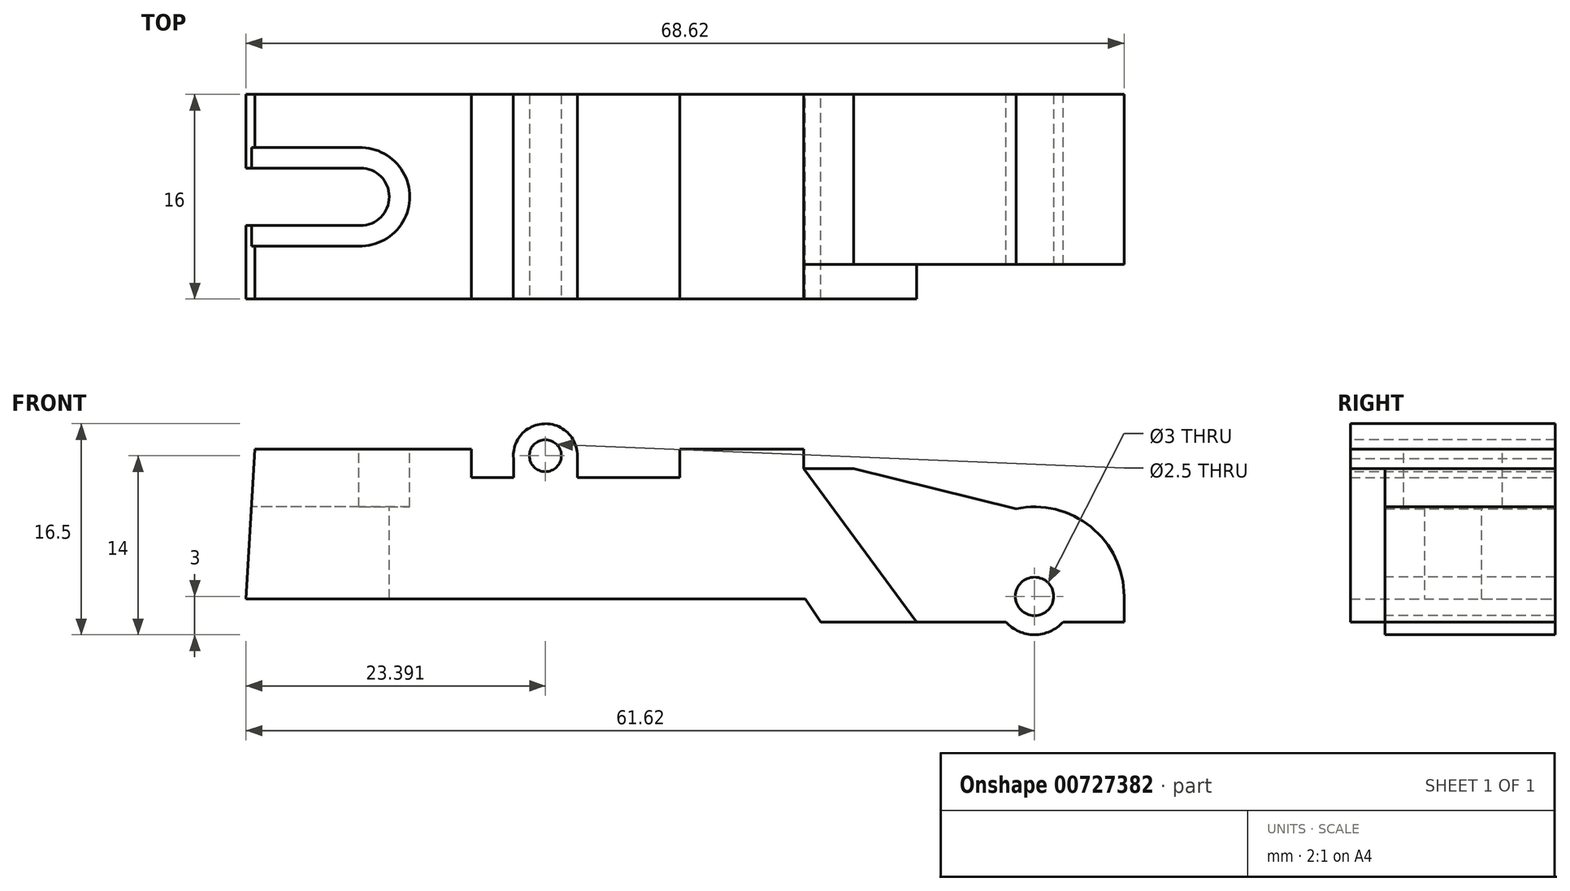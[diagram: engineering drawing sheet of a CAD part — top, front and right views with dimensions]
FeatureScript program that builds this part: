
annotation { "Feature Type Name" : "Feature", "Feature Type Description" : "" }
export const myFeature = defineFeature(function(context is Context, id is Id, definition is map)
    precondition{}
    {
        {
            var Q0;
            Q0=qCreatedBy(makeId("Front.planeOp"),FACE);
            var sketch = newSketch(context, id + "F0", { "sketchPlane" : qUnion([Q0])});
            skLineSegment(sketch, "E0", {"start": v(0, 0) * mm, "end": v(43.7, 0) * mm});
            skLineSegment(sketch, "E1", {"start": v(43.7, 0) * mm, "end": v(44.92, -1.8) * mm});
            skLineSegment(sketch, "E2", {"start": v(44.92, -1.8) * mm, "end": v(59.38, -1.8) * mm});
            skLineSegment(sketch, "E3", {"start": v(68.62, -1.8) * mm, "end": v(68.62, 0.65) * mm});
            skLineSegment(sketch, "E4", {"start": v(47.5, 10.2) * mm, "end": v(43.6, 10.2) * mm});
            skLineSegment(sketch, "E5", {"start": v(43.6, 10.2) * mm, "end": v(43.6, 11.7) * mm});
            skLineSegment(sketch, "E6", {"start": v(43.6, 11.7) * mm, "end": v(33.9, 11.7) * mm});
            skLineSegment(sketch, "E7", {"start": v(33.9, 11.7) * mm, "end": v(33.9, 9.5) * mm});
            skLineSegment(sketch, "E8", {"start": v(33.9, 9.5) * mm, "end": v(25.9, 9.5) * mm});
            skLineSegment(sketch, "E9", {"start": v(25.9, 9.5) * mm, "end": v(25.9, 11.2) * mm});
            skArc(sketch, "E10", {"start": v(25.9, 11.2) * mm, "mid": v(23.28, 13.7) * mm, "end": v(20.9, 10.99) * mm});
            skLineSegment(sketch, "E11", {"start": v(20.9, 10.99) * mm, "end": v(20.9, 9.5) * mm});
            skLineSegment(sketch, "E12", {"start": v(20.9, 9.5) * mm, "end": v(17.6, 9.5) * mm});
            skLineSegment(sketch, "E13", {"start": v(17.6, 9.5) * mm, "end": v(17.6, 11.7) * mm});
            skLineSegment(sketch, "E14", {"start": v(17.6, 11.7) * mm, "end": v(0.7, 11.7) * mm});
            skLineSegment(sketch, "E15", {"start": v(0.7, 11.7) * mm, "end": v(0, 0) * mm});
            skArc(sketch, "E16", {"start": v(68.62, 0.2) * mm, "mid": v(66.03, 5.64) * mm, "end": v(60.18, 7.05) * mm});
            skLineSegment(sketch, "E17", {"start": v(47.5, 10.2) * mm, "end": v(60.18, 7.05) * mm});
            skArc(sketch, "E18", {"start": v(59.38, -1.8) * mm, "mid": v(61.62, -2.8) * mm, "end": v(63.86, -1.8) * mm});
            skLineSegment(sketch, "E19.trimOffspring", {"start": v(63.86, -1.8) * mm, "end": v(68.62, -1.8) * mm});
            skSolve(sketch);
        }
        {
            var Q0;
            Q0=qSketchRegion(id+"F0",true);
            extrude(context, id + "F1", {"entities" : qUnion([Q0]), "depth" : 16 * mm, "offsetDistance" : 25 * mm});
        }
        {
            var Q0;
            Q0=makeQuery(id+"F1.opExtrude","CAP_FACE",FACE,{"disambiguationData":[OSD([sQuery(id+"F0.wireOp",EDGE,"E0"),sQuery(id+"F0.wireOp",EDGE,"E1"),sQuery(id+"F0.wireOp",EDGE,"E2"),sQuery(id+"F0.wireOp",EDGE,"E3"),sQuery(id+"F0.wireOp",EDGE,"E4"),sQuery(id+"F0.wireOp",EDGE,"E5"),sQuery(id+"F0.wireOp",EDGE,"E6"),sQuery(id+"F0.wireOp",EDGE,"E7"),sQuery(id+"F0.wireOp",EDGE,"E8"),sQuery(id+"F0.wireOp",EDGE,"E9"),sQuery(id+"F0.wireOp",EDGE,"E10"),sQuery(id+"F0.wireOp",EDGE,"E11"),sQuery(id+"F0.wireOp",EDGE,"E12"),sQuery(id+"F0.wireOp",EDGE,"E13"),sQuery(id+"F0.wireOp",EDGE,"E14"),sQuery(id+"F0.wireOp",EDGE,"E15"),sQuery(id+"F0.wireOp",EDGE,"E16"),sQuery(id+"F0.wireOp",EDGE,"E17"),sQuery(id+"F0.wireOp",EDGE,"E18"),sQuery(id+"F0.wireOp",EDGE,"E19.trimOffspring")])],"isStart":false});
            var sketch = newSketch(context, id + "F2", { "sketchPlane" : qUnion([Q0])});
            skCircle(sketch, "E20", {"center": v(23.4, 11.2) * mm, "radius": 1.25 * mm});
            skCircle(sketch, "E21", {"center": v(61.62, 0.2) * mm, "radius": 1.5 * mm});
            skSolve(sketch);
        }
        {
            var Q0;
            Q0=makeQuery(id+"F2.imprint","IMPRINT",FACE,{"disambiguationData":[TD([[makeQuery(id+"F2.imprint","IMPRINT",EDGE,{"derivedFrom":sQuery(id+"F2.wireOp",EDGE,"E21")}),1.0]])]});
            var Q1;
            Q1=makeQuery(id+"F2.imprint","IMPRINT",FACE,{"disambiguationData":[TD([[makeQuery(id+"F2.imprint","IMPRINT",EDGE,{"derivedFrom":sQuery(id+"F2.wireOp",EDGE,"E20")}),1.0]])]});
            extrude(context, id + "F3", {"entities" : qUnion([Q0, Q1]), "operationType" : NewBodyOperationType.REMOVE, "endBound" : BoundingType.THROUGH_ALL, "oppositeDirection" : true, "depth" : 25 * mm, "offsetDistance" : 25 * mm});
        }
        {
            var Q0;
            Q0=makeQuery(id+"F1.opExtrude","CAP_FACE",FACE,{"disambiguationData":[OSD([sQuery(id+"F0.wireOp",EDGE,"E0"),sQuery(id+"F0.wireOp",EDGE,"E1"),sQuery(id+"F0.wireOp",EDGE,"E2"),sQuery(id+"F0.wireOp",EDGE,"E3"),sQuery(id+"F0.wireOp",EDGE,"E4"),sQuery(id+"F0.wireOp",EDGE,"E5"),sQuery(id+"F0.wireOp",EDGE,"E6"),sQuery(id+"F0.wireOp",EDGE,"E7"),sQuery(id+"F0.wireOp",EDGE,"E8"),sQuery(id+"F0.wireOp",EDGE,"E9"),sQuery(id+"F0.wireOp",EDGE,"E10"),sQuery(id+"F0.wireOp",EDGE,"E11"),sQuery(id+"F0.wireOp",EDGE,"E12"),sQuery(id+"F0.wireOp",EDGE,"E13"),sQuery(id+"F0.wireOp",EDGE,"E14"),sQuery(id+"F0.wireOp",EDGE,"E15"),sQuery(id+"F0.wireOp",EDGE,"E16"),sQuery(id+"F0.wireOp",EDGE,"E17"),sQuery(id+"F0.wireOp",EDGE,"E18"),sQuery(id+"F0.wireOp",EDGE,"E19.trimOffspring")])],"isStart":false});
            var sketch = newSketch(context, id + "F4", { "sketchPlane" : qUnion([Q0])});
            skLineSegment(sketch, "E22", {"start": v(43.6, 10.2) * mm, "end": v(52.42, -1.8) * mm});
            skLineSegment(sketch, "E23", {"start": v(43.6, 10.2) * mm, "end": v(69.06, 10.2) * mm});
            skLineSegment(sketch, "E24", {"start": v(69.06, 10.2) * mm, "end": v(70.33, -4.38) * mm});
            skLineSegment(sketch, "E25", {"start": v(70.33, -4.38) * mm, "end": v(58.71, -4.38) * mm});
            skLineSegment(sketch, "E26", {"start": v(58.71, -4.38) * mm, "end": v(52.42, -1.8) * mm});
            skSolve(sketch);
        }
        {
            var Q0;
            Q0=qSketchRegion(id+"F4",true);
            extrude(context, id + "F5", {"entities" : qUnion([Q0]), "operationType" : NewBodyOperationType.REMOVE, "oppositeDirection" : true, "depth" : 2.7 * mm, "offsetDistance" : 25 * mm});
        }
        {
            var Q0;
            Q0=qCreatedBy(makeId("Front.planeOp"),FACE);
            cPlane(context, id + "F6", {"entities" : qUnion([Q0]), "cplaneType" : CPlaneType.OFFSET, "offset" : 8 * mm, "width" : 150 * mm, "height" : 150 * mm});
        }
        {
            var Q0;
            Q0=makeQuery(id+"F1.opExtrude","SWEPT_FACE",FACE,{"disambiguationData":[OSD([sQuery(id+"F0.wireOp",EDGE,"E14")])]});
            var sketch = newSketch(context, id + "F7", { "sketchPlane" : qUnion([Q0])});
            skLineSegment(sketch, "E27", {"start": v(0.7, -5.75) * mm, "end": v(8.94, -5.75) * mm});
            skLineSegment(sketch, "E28", {"start": v(0.7, -8) * mm, "end": v(68.7, -8) * mm, "construction": true});
            skPoint(sketch, "E29.third.point", {"position": v(6.72, -12.54) * mm});
            skLineSegment(sketch, "E30", {"start": v(8.94, -10.25) * mm, "end": v(0.7, -10.25) * mm});
            skArc(sketch, "E31", {"start": v(8.94, -10.25) * mm, "mid": v(11.2, -8) * mm, "end": v(8.94, -5.75) * mm});
            skPoint(sketch, "E32.orphan", {"position": v(8.91, -5.75) * mm});
            skLineSegment(sketch, "E33", {"start": v(0.7, -5.75) * mm, "end": v(-0.9, -5.75) * mm});
            skLineSegment(sketch, "E34", {"start": v(-0.9, -5.75) * mm, "end": v(-0.9, -10.25) * mm});
            skLineSegment(sketch, "E35", {"start": v(-0.9, -10.25) * mm, "end": v(0.7, -10.25) * mm});
            skSolve(sketch);
        }
        {
            var Q0;
            {var subQ0=sQuery(id+"F7.wireOp",EDGE,"E27");Q0=makeQuery(id+"F7.imprint","IMPRINT",FACE,{"disambiguationData":[TD([[makeQuery(id+"F7.imprint","IMPRINT",EDGE,{"derivedFrom":subQ0}),-1.0]])]});}
            extrude(context, id + "F8", {"entities" : qUnion([Q0]), "operationType" : NewBodyOperationType.REMOVE, "endBound" : BoundingType.THROUGH_ALL, "oppositeDirection" : true, "depth" : 25 * mm, "offsetDistance" : 25 * mm});
        }
        {
            var Q0;
            Q0=qSketchRegion(id+"F7",true);
            extrude(context, id + "F9", {"entities" : qUnion([Q0]), "operationType" : NewBodyOperationType.REMOVE, "oppositeDirection" : true, "depth" : 25 * mm, "offsetDistance" : 25 * mm});
        }
        {
            var Q0;
            Q0=makeQuery(id+"F1.opExtrude","SWEPT_FACE",FACE,{"disambiguationData":[OSD([sQuery(id+"F0.wireOp",EDGE,"E14")])]});
            var sketch = newSketch(context, id + "F10", { "sketchPlane" : qUnion([Q0])});
            skCircle(sketch, "E36", {"center": v(8.94, -8) * mm, "radius": 3.85 * mm});
            skLineSegment(sketch, "E37", {"start": v(9.06, -4.15) * mm, "end": v(-1.52, -4.15) * mm});
            skLineSegment(sketch, "E38", {"start": v(9.06, -11.85) * mm, "end": v(-2.62, -11.85) * mm});
            skLineSegment(sketch, "E39", {"start": v(-2.62, -11.85) * mm, "end": v(-1.52, -4.15) * mm});
            skSolve(sketch);
        }
        {
            var Q0;
            Q0=qSketchRegion(id+"F10",true);
            extrude(context, id + "F11", {"entities" : qUnion([Q0]), "operationType" : NewBodyOperationType.REMOVE, "oppositeDirection" : true, "depth" : 4.5 * mm, "offsetDistance" : 25 * mm});
        }
    });
